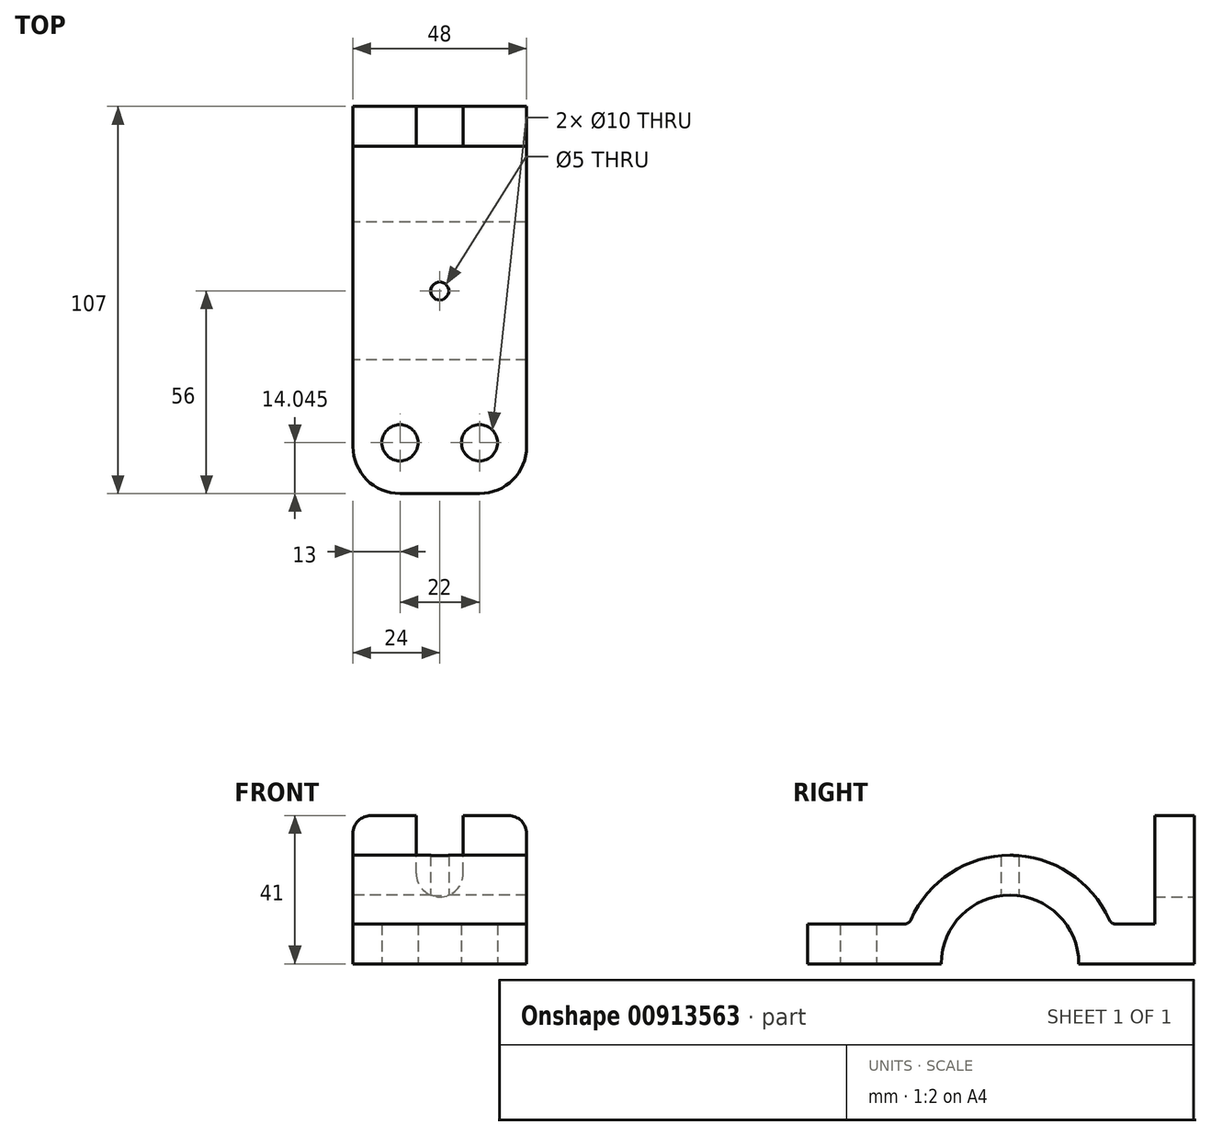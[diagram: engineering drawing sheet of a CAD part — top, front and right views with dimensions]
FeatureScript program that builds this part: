
annotation { "Feature Type Name" : "Feature", "Feature Type Description" : "" }
export const myFeature = defineFeature(function(context is Context, id is Id, definition is map)
    precondition{}
    {
        {
            var Q0;
            Q0=qCreatedBy(makeId("Right.planeOp"),FACE);
            var sketch = newSketch(context, id + "F0", { "sketchPlane" : qUnion([Q0])});
            skCircle(sketch, "E0", {"center": v(0, 0) * mm, "radius": 19 * mm});
            skCircle(sketch, "E1", {"center": v(0, 0) * mm, "radius": 30 * mm});
            skLineSegment(sketch, "E2.bottom", {"start": v(-56, 0) * mm, "end": v(51, 0) * mm});
            skLineSegment(sketch, "E2.top", {"start": v(-56, 11) * mm, "end": v(51, 11) * mm});
            skLineSegment(sketch, "E2.left", {"start": v(-56, 0) * mm, "end": v(-56, 11) * mm});
            skLineSegment(sketch, "E2.right", {"start": v(51, 0) * mm, "end": v(51, 11) * mm});
            skLineSegment(sketch, "E3.bottom", {"start": v(51, 11) * mm, "end": v(40, 11) * mm});
            skLineSegment(sketch, "E3.top", {"start": v(51, 41) * mm, "end": v(40, 41) * mm});
            skLineSegment(sketch, "E3.left", {"start": v(51, 11) * mm, "end": v(51, 41) * mm});
            skLineSegment(sketch, "E3.right", {"start": v(40, 11) * mm, "end": v(40, 41) * mm});
            skSolve(sketch);
        }
        {
            var Q0;
            {var subQ5=sQuery(id+"F0.wireOp",EDGE,"E2.left");Q0=makeQuery(id+"F0.imprint","IMPRINT",FACE,{"disambiguationData":[TD([[makeQuery(id+"F0.imprint","IMPRINT",EDGE,{"derivedFrom":subQ5}),-1.0]])]});}
            var Q1;
            {var subQ0=sQuery(id+"F0.wireOp",EDGE,"E2.bottom");var subQ1=sQuery(id+"F0.wireOp",EDGE,"E0");var subQ2=makeQuery(id+"F0.imprint","INTERSECT",VERTEX,{"disambiguationData":[OD(0.0)],"derivedFrom":[subQ1,subQ0]});Q1=makeQuery(id+"F0.imprint","IMPRINT",FACE,{"disambiguationData":[TD([[makeQuery(id+"F0.imprint","IMPRINT",EDGE,{"disambiguationData":[TD([[subQ2,1.0]])],"derivedFrom":subQ1}),-1.0]])]});}
            var Q2;
            {var subQ0=sQuery(id+"F0.wireOp",EDGE,"E2.top");var subQ1=sQuery(id+"F0.wireOp",EDGE,"E0");var subQ2=makeQuery(id+"F0.imprint","INTERSECT",VERTEX,{"disambiguationData":[OD(0.0)],"derivedFrom":[subQ1,subQ0]});Q2=makeQuery(id+"F0.imprint","IMPRINT",FACE,{"disambiguationData":[TD([[makeQuery(id+"F0.imprint","IMPRINT",EDGE,{"disambiguationData":[TD([[subQ2,1.0]])],"derivedFrom":subQ1}),-1.0]])]});}
            var Q3;
            {var subQ0=sQuery(id+"F0.wireOp",EDGE,"E2.top");var subQ1=sQuery(id+"F0.wireOp",EDGE,"E0");var subQ2=makeQuery(id+"F0.imprint","INTERSECT",VERTEX,{"disambiguationData":[OD(1.0)],"derivedFrom":[subQ1,subQ0]});Q3=makeQuery(id+"F0.imprint","IMPRINT",FACE,{"disambiguationData":[TD([[makeQuery(id+"F0.imprint","IMPRINT",EDGE,{"disambiguationData":[TD([[subQ2,1.0]])],"derivedFrom":subQ1}),-1.0]])]});}
            var Q4;
            {var subQ0=sQuery(id+"F0.wireOp",EDGE,"E2.right");Q4=makeQuery(id+"F0.imprint","IMPRINT",FACE,{"disambiguationData":[TD([[makeQuery(id+"F0.imprint","IMPRINT",EDGE,{"derivedFrom":subQ0}),1.0]])]});}
            var Q5;
            Q5=makeQuery(id+"F0.imprint","IMPRINT",FACE,{"disambiguationData":[TD([[makeQuery(id+"F0.imprint","IMPRINT",EDGE,{"derivedFrom":sQuery(id+"F0.wireOp",EDGE,"E3.top")}),1.0]])]});
            var Q6;
            Q6 = qSketchRegion(id + "F2", true);
            extrude(context, id + "F1", {"entities" : qUnion([Q0, Q1, Q2, Q3, Q4, Q5, Q6]), "endBound" : BoundingType.SYMMETRIC, "depth" : 48 * mm, "offsetDistance" : 25 * mm});
        }
        {
            var Q0;
            Q0=makeQuery(id+"F1.opExtrude","SWEPT_FACE",FACE,{"disambiguationData":[OSD([sQuery(id+"F0.wireOp",EDGE,"E2.right"),sQuery(id+"F0.wireOp",EDGE,"E3.left")])]});
            var sketch = newSketch(context, id + "F2", { "sketchPlane" : qUnion([Q0])});
            skLineSegment(sketch, "E4", {"start": v(0, 0) * mm, "end": v(0, 41) * mm, "construction": true});
            skCircle(sketch, "E5", {"center": v(0, 25) * mm, "radius": 6.5 * mm});
            skLineSegment(sketch, "E6", {"start": v(-6.5, 25) * mm, "end": v(-6.5, 41) * mm});
            skLineSegment(sketch, "E7", {"start": v(6.5, 25) * mm, "end": v(6.5, 41) * mm});
            skSolve(sketch);
        }
        {
            var Q0;
            {var subQ0=sQuery(id+"F2.wireOp",EDGE,"E5");var subQ2=makeQuery(id+"F2.imprint","INTERSECT",VERTEX,{"derivedFrom":[subQ0,sQuery(id+"F2.wireOp",EDGE,"E6")]});Q0=makeQuery(id+"F2.imprint","IMPRINT",FACE,{"disambiguationData":[TD([[makeQuery(id+"F2.imprint","IMPRINT",EDGE,{"disambiguationData":[TD([[subQ2,1.0]])],"derivedFrom":subQ0}),1.0]])]});}
            var Q1;
            {var subQ2=sQuery(id+"F2.wireOp",EDGE,"E6");Q1=makeQuery(id+"F2.imprint","IMPRINT",FACE,{"disambiguationData":[TD([[makeQuery(id+"F2.imprint","IMPRINT",EDGE,{"derivedFrom":subQ2}),-1.0]])]});}
            var Q2;
            Q2=makeQuery(id+"F1.opExtrude","SWEPT_FACE",FACE,{"disambiguationData":[OSD([sQuery(id+"F0.wireOp",EDGE,"E3.right")])]});
            extrude(context, id + "F3", {"entities" : qUnion([Q0, Q1]), "operationType" : NewBodyOperationType.REMOVE, "endBound" : BoundingType.UP_TO_SURFACE, "oppositeDirection" : true, "endBoundEntityFace" : qUnion([Q2]), "offsetDistance" : 25 * mm, "depth" : 25 * mm});
        }
        {
            var Q0;
            Q0=qCreatedBy(makeId("Top.planeOp"),FACE);
            var sketch = newSketch(context, id + "F4", { "sketchPlane" : qUnion([Q0])});
            skCircle(sketch, "E8", {"center": v(0, 0) * mm, "radius": 2.5 * mm});
            skLineSegment(sketch, "E9", {"start": v(24, -41.96) * mm, "end": v(-24, -41.96) * mm, "construction": true});
            skLineSegment(sketch, "E10", {"start": v(0, -56) * mm, "end": v(0, -27.91) * mm, "construction": true});
            skCircle(sketch, "E11", {"center": v(-11, -41.96) * mm, "radius": 5 * mm});
            skCircle(sketch, "E12", {"center": v(11, -41.96) * mm, "radius": 5 * mm});
            skSolve(sketch);
        }
        {
            var Q0;
            Q0=qSketchRegion(id+"F4",true);
            extrude(context, id + "F5", {"entities" : qUnion([Q0]), "operationType" : NewBodyOperationType.REMOVE, "endBound" : BoundingType.THROUGH_ALL, "depth" : 25 * mm});
        }
        {
            var Q0;
            Q0=makeQuery(id+"F1.opExtrude","CAP_EDGE",EDGE,{"disambiguationData":[OSD([sQuery(id+"F0.wireOp",EDGE,"E2.left")])],"isStart":false});
            var Q1;
            Q1=makeQuery(id+"F1.opExtrude","CAP_EDGE",EDGE,{"disambiguationData":[OSD([sQuery(id+"F0.wireOp",EDGE,"E2.left")])],"isStart":true});
            fillet(context, id + "F6", {"entities" : qUnion([Q0, Q1]), "radius" : 13 * mm, "tangentPropagation" : true, "allowEdgeOverflow" : false});
        }
        {
            var Q0;
            Q0=makeQuery(id+"F1.opExtrude","CAP_EDGE",EDGE,{"disambiguationData":[OSD([sQuery(id+"F0.wireOp",EDGE,"E3.top")])],"isStart":false});
            var Q1;
            Q1=makeQuery(id+"F1.opExtrude","CAP_EDGE",EDGE,{"disambiguationData":[OSD([sQuery(id+"F0.wireOp",EDGE,"E3.top")])],"isStart":true});
            fillet(context, id + "F7", {"entities" : qUnion([Q0, Q1]), "radius" : 5 * mm, "tangentPropagation" : true, "allowEdgeOverflow" : false});
        }
        {
            var Q0;
            {var subQ0=sQuery(id+"F0.wireOp",EDGE,"E2.top");var subQ1=sQuery(id+"F0.wireOp",EDGE,"E1");Q0=makeQuery(id+"F1.opExtrude","SWEPT_EDGE",EDGE,{"disambiguationData":[OSD([subQ1,subQ0]),TDD([makeQuery(id+"F0.imprint","INTERSECT",VERTEX,{"disambiguationData":[OD(1.0)],"derivedFrom":[subQ1,subQ0]})])]});}
            var Q1;
            {var subQ0=sQuery(id+"F0.wireOp",EDGE,"E2.top");var subQ1=sQuery(id+"F0.wireOp",EDGE,"E1");Q1=makeQuery(id+"F1.opExtrude","SWEPT_EDGE",EDGE,{"disambiguationData":[OSD([subQ1,subQ0]),TDD([makeQuery(id+"F0.imprint","INTERSECT",VERTEX,{"disambiguationData":[OD(0.0)],"derivedFrom":[subQ1,subQ0]})])]});}
            fillet(context, id + "F8", {"entities" : qUnion([Q0, Q1]), "radius" : 2 * mm, "tangentPropagation" : true, "allowEdgeOverflow" : false});
        }
    });
